# Revit family: КОМ-ВО_Eng
name_source: partatom
category: Duct Accessories
units: mm (PartAtom-declared; Revit-internal decimal feet)

## family parameters
Always vertical = Yes
Cut with Voids When Loaded = No
Part Type = Attaches To
Round Connector Dimension = Use Diameter
Shared = No
Work Plane-Based = No

## types (11) — shared parameters
00_20_Manufacturer = Vents
00_20_Name = Backdraft damper
Casing Material = Metal, painted, blue, matte RAL 5007
Load Classification = HVAC
Maintenance zone material = <By Category>
Manufacturer = Vents
URL = https://ventilation-system.com
zero-valued in all types: Default Elevation

## per-type parameters (varying)
| type | D1 | D2 | Diameter | Dn | Dy | L | Length | R1 | Weight | d | l | n | t |
| KOM-VO-400 | 450 mm  [stored 1.47638 ft] | 490 mm  [stored 1.60761 ft] | 490 mm  [stored 1.60761 ft] | 410 mm  [stored 1.34514 ft] | 400 mm  [stored 1.31234 ft] | 250 mm  [stored 0.82021 ft] | 250 mm  [stored 0.82021 ft] | 225 mm  [stored 0.738189 ft] | 5.40 kg | 8 mm  [stored 0.0262467 ft] | 125 mm  [stored 0.410105 ft] | 12 | 245 mm  [stored 0.803806 ft] |
| KOM-VO-450 | 500 mm  [stored 1.64042 ft] | 540 mm  [stored 1.77165 ft] | 540 mm  [stored 1.77165 ft] | 460 mm | 450 mm  [stored 1.47638 ft] | 250 mm  [stored 0.82021 ft] | 250 mm  [stored 0.82021 ft] | 250 mm  [stored 0.82021 ft] | 6.20 kg | 8 mm  [stored 0.0262467 ft] | 125 mm  [stored 0.410105 ft] | 12 | 245 mm  [stored 0.803806 ft] |
| KOM-VO-500 | 560 mm  [stored 1.83727 ft] | 590 mm  [stored 1.9357 ft] | 590 mm  [stored 1.9357 ft] | 510 mm | 500 mm  [stored 1.64042 ft] | 250 mm  [stored 0.82021 ft] | 250 mm  [stored 0.82021 ft] | 280 mm  [stored 0.918635 ft] | 7.10 kg | 12 mm  [stored 0.0393701 ft] | 125 mm  [stored 0.410105 ft] | 12 | 245 mm  [stored 0.803806 ft] |
| KOM-VO-560 | 620 mm  [stored 2.03412 ft] | 650 mm | 650 mm | 570 mm  [stored 1.87008 ft] | 560 mm  [stored 1.83727 ft] | 320 mm  [stored 1.04987 ft] | 320 mm  [stored 1.04987 ft] | 310 mm  [stored 1.01706 ft] | 9.60 kg | 12 mm  [stored 0.0393701 ft] | 160 mm  [stored 0.524934 ft] | 12 | 315 mm  [stored 1.03346 ft] |
| KOM-VO-630 | 690 mm | 720 mm | 720 mm | 640 mm  [stored 2.09974 ft] | 630 mm  [stored 2.06693 ft] | 370 mm  [stored 1.21391 ft] | 370 mm  [stored 1.21391 ft] | 345 mm  [stored 1.13189 ft] | 14.20 kg | 12 mm  [stored 0.0393701 ft] | 185 mm  [stored 0.606955 ft] | 12 | 365 mm  [stored 1.19751 ft] |
| KOM-VO-710 | 770 mm | 810 mm | 810 mm | 720 mm | 710 mm | 390 mm  [stored 1.27953 ft] | 390 mm  [stored 1.27953 ft] | 385 mm  [stored 1.26312 ft] | 21.40 kg | 12 mm  [stored 0.0393701 ft] | 195 mm  [stored 0.639764 ft] | 16 | 385 mm  [stored 1.26312 ft] |
| KOM-VO-800 | 860 mm | 900 mm | 900 mm | 810 mm | 800 mm | 390 mm  [stored 1.27953 ft] | 390 mm  [stored 1.27953 ft] | 430 mm | 25.40 kg | 12 mm  [stored 0.0393701 ft] | 195 mm  [stored 0.639764 ft] | 16 | 385 mm  [stored 1.26312 ft] |
| KOM-VO-900 | 970 mm | 1010 mm | 1010 mm | 910 mm | 900 mm | 450 mm  [stored 1.47638 ft] | 450 mm  [stored 1.47638 ft] | 485 mm  [stored 1.59121 ft] | 32.60 kg | 15 mm  [stored 0.0492126 ft] | 225 mm  [stored 0.738189 ft] | 16 | 445 mm  [stored 1.45997 ft] |
| KOM-VO-1000 | 1070 mm | 1110 mm | 1110 mm | 1010 mm | 1000 mm | 450 mm  [stored 1.47638 ft] | 450 mm  [stored 1.47638 ft] | 535 mm  [stored 1.75525 ft] | 36.90 kg | 15 mm  [stored 0.0492126 ft] | 225 mm  [stored 0.738189 ft] | 16 | 445 mm  [stored 1.45997 ft] |
| KOM-VO-1120 | 1190 mm | 1260 mm | 1260 mm | 1130 mm | 1120 mm | 540 mm  [stored 1.77165 ft] | 540 mm  [stored 1.77165 ft] | 595 mm  [stored 1.9521 ft] | 59.50 kg | 15 mm  [stored 0.0492126 ft] | 270 mm  [stored 0.885827 ft] | 20 | 535 mm  [stored 1.75525 ft] |
| KOM-VO-1250 | 1320 mm | 1390 mm | 1390 mm | 1260 mm | 1250 mm | 540 mm  [stored 1.77165 ft] | 540 mm  [stored 1.77165 ft] | 660 mm | 67.40 kg | 15 mm  [stored 0.0492126 ft] | 270 mm  [stored 0.885827 ft] | 20 | 535 mm  [stored 1.75525 ft] |

note: column(s) folded — value = type name in every type: 00_20_Type

note: [stored X ft] marks values corroborated as IEEE doubles in the binary element streams (Revit-internal decimal feet)
